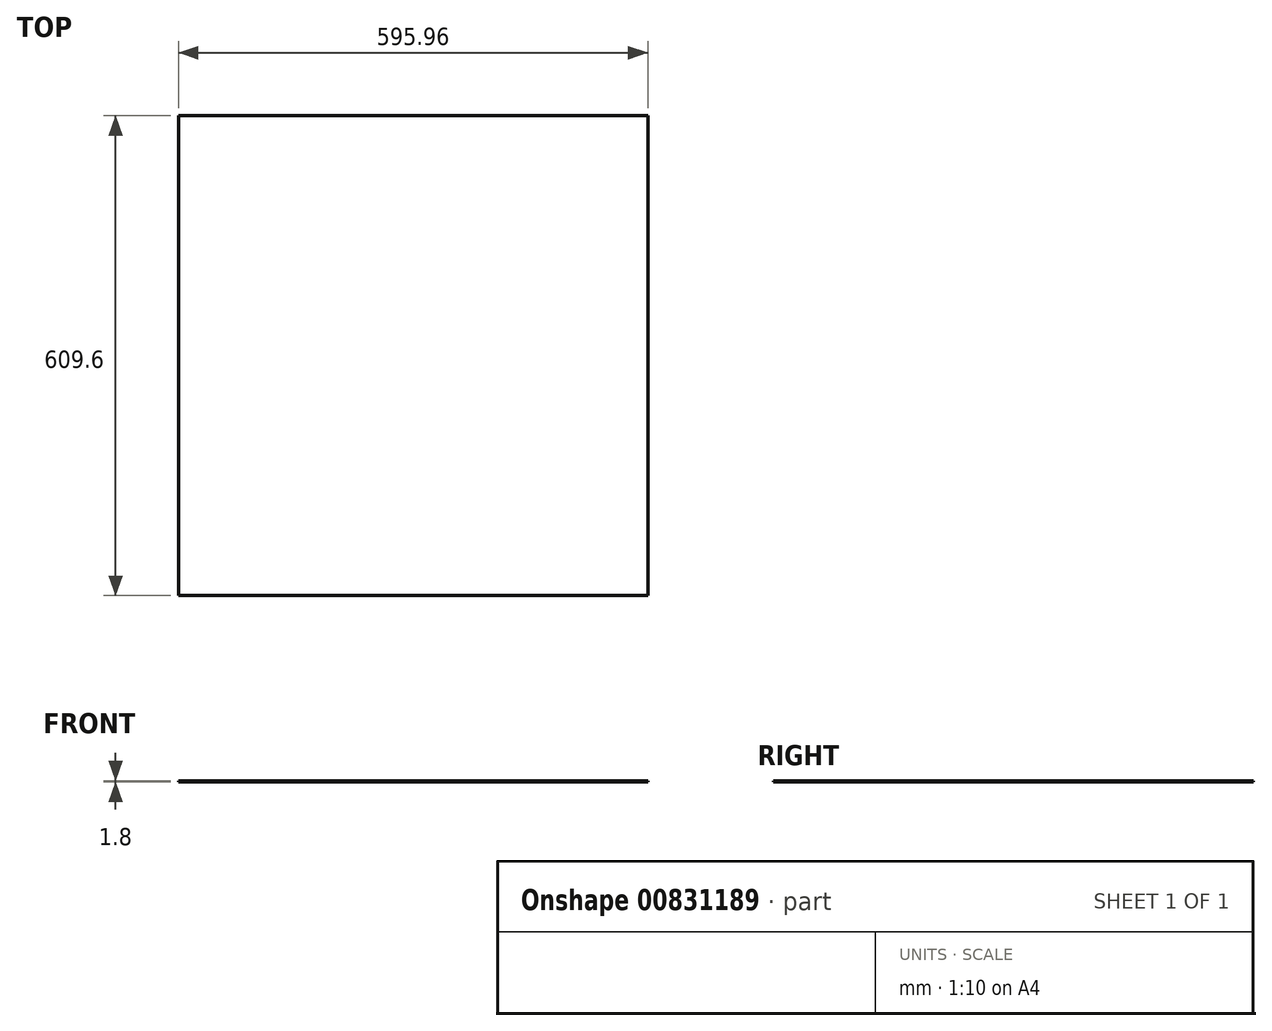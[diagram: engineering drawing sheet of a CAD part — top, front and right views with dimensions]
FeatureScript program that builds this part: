
annotation { "Feature Type Name" : "Feature", "Feature Type Description" : "" }
export const myFeature = defineFeature(function(context is Context, id is Id, definition is map)
    precondition{}
    {
        {
            var Q0;
            Q0=qCreatedBy(makeId("Top.planeOp"),FACE);
            var sketch = newSketch(context, id + "F0", { "sketchPlane" : qUnion([Q0])});
            skLineSegment(sketch, "E0.bottom", {"start": v(297.98, 304.8) * mm, "end": v(-297.98, 304.8) * mm});
            skLineSegment(sketch, "E0.top", {"start": v(297.98, -304.8) * mm, "end": v(-297.98, -304.8) * mm});
            skLineSegment(sketch, "E0.left", {"start": v(297.98, 304.8) * mm, "end": v(297.98, -304.8) * mm});
            skLineSegment(sketch, "E0.right", {"start": v(-297.98, 304.8) * mm, "end": v(-297.98, -304.8) * mm});
            skPoint(sketch, "E0.middle", {"position": v(0, 0) * mm});
            skSolve(sketch);
        }
        {
            var Q0;
            Q0 = qSketchRegion(id + "F0", true);
            extrude(context, id + "F1", {"entities" : qUnion([Q0]), "depth" : 1.8 * mm, "offsetDistance" : 25 * mm});
        }
    });
